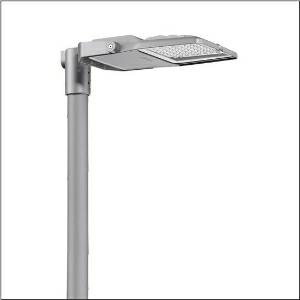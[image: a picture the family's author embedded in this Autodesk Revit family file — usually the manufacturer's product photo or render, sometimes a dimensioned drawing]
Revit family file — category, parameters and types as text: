
# Revit family: floodlight_fl_21_mini___pl52_5xa7775c2d3a_b3eb
name_source: partatom
category: Lighting Fixtures
units: mm (PartAtom-declared; Revit-internal decimal feet)

## family parameters
Cut with Voids When Loaded = No
Host = Face
Light Source = No
Part Type = Normal
Room Calculation Point = No
Round Connector Dimension = Use Diameter
Shared = No

## types (1)
- --- (1 x LED, 12190 lm, 89 W, 3000K)
    Apparent Load = 89 VA
    CIE Flux Codes = 26 60 98 100 100
    Color Rendering = 70
    Color Temperature = 3000K
    Default Elevation = 1800 mm
    Description = Floodlight FL 21 mini, floodlight, primary light control with lens, of PMMA, primary optical cover: protective disc, of toughened safety glass, transparent, light distribution: PL52, light emission: direct distribution, installation type: surface-mounted, LED, High Power LED, rated luminous flux: 12.190lm, luminous efficacy: 137lm/W, light colour: 730, colour temperature: 3000K, control gear: Smart Interface (Zhaga), control: flexible luminous flux parameterisation, time-dependent luminous flux control, constant luminous flux control, overheat protection, pre-setting: logarithmic dimming characteristic, with terminal, 6-pole, mains connection: 220..240V, AC, 50/60Hz, start of lifetime: 89W, end of service life: 94W, reduction: 43W, luminaire housing, of diecast aluminium, powder-coated, Siteco® metallic grey (DB 702S), corrosivity category C5 mid according to DIN EN ISO 12944, suitable for swimming pools, chlorine-resistant, sealing non-destructively replaceable, please order mast flange separately, mast bracket, of steel, galvanised, powder-coated, Siteco® metallic grey (DB 702S), Smart Interface above, protection rating (complete): IP66, insulation class (complete): insulation class II (safety insulation), certification: CE, ENEC, VDE, protection symbol: D, impact resistance: IK08, permissible operating ambient temperature: -40..+40°C, permissible operating ambient temperature for outdoor applications: -40..+50°C, standard: DIN EN 12944, LABS conformity tested according to VDMA 24364:2018-05, packaging unit: 1 piece

Light Distribution: PL52
    Height = 70 mm
    Lamp = 1 x LED
    Lamp Light Flux = 12190 lm
    Lamp Power = 89 W
    Lamp count = 1
    Length = 485 mm
    Luminous efficacy = 137 lm/W
    Manufacturer = Siteco
    ModVariant = No
    Model = 5XA7775C2D3A
    Number of Poles = 1
    OnlyDefault = Yes
    Power Factor = 1
    Product Name = Floodlight FL 21 mini | PL52
    Product group = floodlight | pylon annexe
    ProductGroupID = 6200
    Protection Class = Protection class II
    Protection Degree = IP 66
    RLX_Detail_Level = 1
    RLX_Emergency_Light_Flux = 0 lm
    RLX_Emergency_Type = 0
    RLX_Emergency_Type_DB = No
    RlxData = <blob elided: 101097 chars, md5=df329b4c>
    Socket = socket
    Standby Power = 0 W
    System Light Flux = 12190 lm
    System Power = 89 W
    Type Comments = factory setting: luminous flux: 100 % | dim-lin: 254 | 456 mA
    Type Image = l_1007125.jpg
    URL = http://relux.com
    VarID = @adj_163322
    Voltage = 0 V
    Weight = 0.00 kg
    Width = 337 mm

## geometry (parser evidence)
native form markers: Blend x4, Sweep x12
no freeform markers — native parametric forms only
